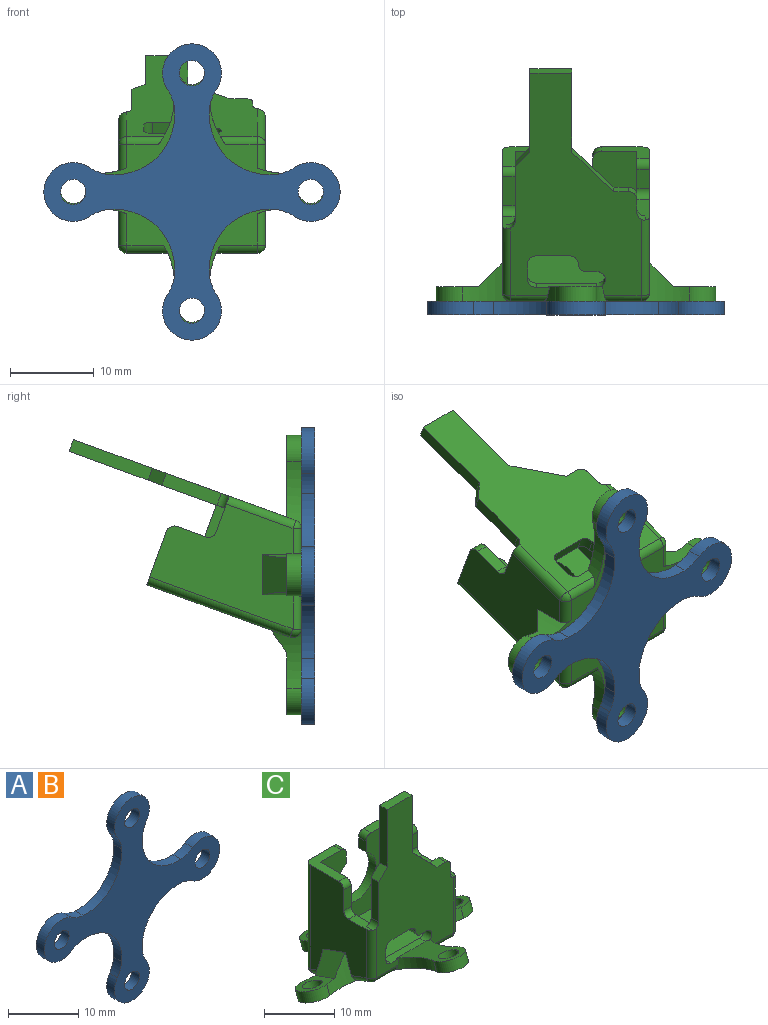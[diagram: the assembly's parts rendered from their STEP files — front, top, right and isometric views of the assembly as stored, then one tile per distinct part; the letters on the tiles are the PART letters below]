
ASSEMBLY  parts=3 mates=1
PART A: 22 faces, bbox 35.3x1.6x35.3 mm
  f0: cylinder r=5mm len=2.39mm, axis (0,1,0), area 4.1mm2, adj f1,f19,f20,f21
  f1: cylinder r=3.5mm len=7mm, axis (0,1,0), area 24.2mm2, adj f0,f2,f20,f21
  f2: cylinder r=5mm len=2.39mm, axis (0,1,0), area 4.1mm2, adj f1,f3,f20,f21
  f3: cylinder r=7.18mm len=7.75mm, axis (0,1,0), area 19.9mm2, adj f2,f4,f20,f21
  f4: cylinder r=5mm len=2.39mm, axis (0,1,0), area 4.1mm2, adj f3,f5,f20,f21
  f5: cylinder r=3.5mm len=7mm, axis (0,1,0), area 24.2mm2, adj f4,f6,f20,f21
  f6: cylinder r=5mm len=2.39mm, axis (0,1,0), area 4.1mm2, adj f5,f7,f20,f21
  f7: cylinder r=7.18mm len=7.75mm, axis (0,1,0), area 19.9mm2, adj f6,f8,f20,f21
  f8: cylinder r=5mm len=2.39mm, axis (0,1,0), area 4.1mm2, adj f7,f9,f20,f21
  f9: cylinder r=3.5mm len=7mm, axis (0,1,0), area 24.2mm2, adj f8,f10,f20,f21
  f10: cylinder r=5mm len=2.39mm, axis (0,1,0), area 4.1mm2, adj f9,f11,f20,f21
  f11: cylinder r=7.18mm len=7.75mm, axis (0,1,0), area 19.9mm2, adj f10,f12,f20,f21
  f12: cylinder r=5mm len=2.39mm, axis (0,1,0), area 4.1mm2, adj f11,f13,f20,f21
  f13: cylinder r=3.5mm len=7mm, axis (0,1,0), area 24.2mm2, adj f12,f14,f20,f21
  f14: cylinder r=5mm len=2.39mm, axis (0,1,0), area 4.1mm2, adj f13,f19,f20,f21
  f15: cylinder r=1.5mm len=3mm, axis (0,1,0), area 15.1mm2, adj f20,f21
  f16: cylinder r=1.5mm len=3mm, axis (0,1,0), area 15.1mm2, adj f20,f21
  f17: cylinder r=1.5mm len=3mm, axis (0,1,0), area 15.1mm2, adj f20,f21
  f18: cylinder r=1.5mm len=3mm, axis (0,1,0), area 15.1mm2, adj f20,f21
  f19: cylinder r=7.18mm len=7.75mm, axis (0,1,0), area 19.9mm2, adj f0,f14,f20,f21
  f20: plane 35.28x35.28mm, normal (0,-1,0), area 333.8mm2, adj f0,f1,f2,f3,f4,f5,f6,f7
  f21: plane 35.28x35.28mm, normal (0,1,0), area 333.8mm2, adj f0,f1,f2,f3,f4,f5,f6,f7
PART B: same geometry as A
PART C: 84 faces, bbox 33.3x31.9x36.7 mm
  f0: plane 18.14x11.25mm, normal (-1,0,0), area 138.6mm2, adj f8,f21,f22,f36,f37,f44,f45,f64
  f1: plane 28.19x15.51mm, normal (0,-1,0), area 258.5mm2, adj f4,f5,f6,f17,f20,f23,f24,f25
  f2: plane 18.18x15.53mm, normal (0,1,0), area 205.4mm2, adj f8,f9,f14,f15,f16,f41,f42,f43
  f3: plane 18.14x11.25mm, normal (1,0,0), area 131.4mm2, adj f9,f18,f19,f38,f39,f40,f43,f57
  f4: plane 7.25x1.5mm, normal (0,0,1), area 9.1mm2, adj f1,f5,f7,f35,f51,f52
  f5: cylinder r=1mm len=2mm, axis (0,-1,0), area 4.6mm2, adj f1,f4,f7,f25,f51
  f6: plane 1.75x1.5mm, normal (0,0,1), area 2.6mm2, adj f1,f7,f29,f48
  f7: plane 27.38x16.5mm, normal (0,1,0), area 244.8mm2, adj f4,f5,f6,f11,f12,f13,f17,f18
  f8: plane 6.75x5.75mm, normal (0,0,1), area 16.3mm2, adj f0,f2,f10,f12,f37,f41,f44
  f9: plane 5.75x4.05mm, normal (0,0,1), area 12.2mm2, adj f2,f3,f10,f11,f40,f42,f43
  f10: plane 14.5x13.25mm, normal (0,-1,0), area 131.3mm2, adj f8,f9,f11,f12,f13,f14,f15,f16
  f11: plane 13.25x10.25mm, normal (-1,0,0), area 105.7mm2, adj f7,f9,f10,f13,f18,f19,f39,f40
  f12: plane 13.25x10.25mm, normal (1,0,0), area 113.4mm2, adj f7,f8,f10,f13,f21,f22,f36,f37
  f13: plane 14.5x10.25mm, normal (0,0,1), area 148.6mm2, adj f7,f10,f11,f12
  f14: cylinder r=4mm len=8mm, axis (0,1,0), area 31.4mm2, adj f2,f10,f15,f16
  f15: plane 1.89x1.5mm, normal (-1,0,0), area 2.8mm2, adj f2,f10,f14,f42
  f16: plane 1.89x1.5mm, normal (1,0,0), area 2.8mm2, adj f2,f10,f14,f41
  f17: plane 1.63x1.5mm, normal (1,0,0), area 2.4mm2, adj f1,f7,f47,f48
  f18: plane 7.07x1.5mm, normal (0,0,1), area 9.1mm2, adj f3,f7,f11,f38,f39,f47
  f19: plane 2.5x1.5mm, normal (0,-1,0), area 3.8mm2, adj f3,f11,f39,f40
  f20: plane 6.98x1.5mm, normal (-1,0,0), area 10.5mm2, adj f1,f7,f30,f46
  f21: plane 3.6x1.5mm, normal (0,-1,0), area 5.4mm2, adj f0,f12,f36,f37
  f22: plane 4.37x1.5mm, normal (0,0,1), area 5.1mm2, adj f0,f7,f12,f36,f45,f46
  f23: plane 4x1.5mm, normal (0,0,-1), area 6mm2, adj f1,f7,f33,f34
  f24: plane 2x1.5mm, normal (1,0,0), area 3mm2, adj f1,f7,f34,f35
  f25: plane 1.5x1.25mm, normal (0,0,-1), area 1.9mm2, adj f1,f5,f7,f32
  f26: plane 10x1.5mm, normal (1,0,0), area 15mm2, adj f1,f7,f28,f29
  f27: plane 10x1.5mm, normal (-1,0,0), area 15mm2, adj f1,f7,f28,f30
  f28: plane 5x1.5mm, normal (0,0,1), area 7.5mm2, adj f1,f7,f26,f27
  f29: plane 5x5mm, normal (0.71,0,0.71), area 10.6mm2, adj f1,f6,f7,f26
  f30: plane 1.75x1.75mm, normal (-0.71,0,0.71), area 3.7mm2, adj f1,f7,f20,f27
  f31: plane 33.28x31.28mm, normal (0,-0.34,-0.94), area 335.5mm2, adj f49,f50,f52,f53,f54,f55,f57,f58
  f32: cylinder r=1mm len=1.5mm, axis (0,-1,0), area 2.4mm2, adj f1,f7,f25,f33
  f33: cylinder r=1mm len=1.5mm, axis (0,1,0), area 2.4mm2, adj f1,f7,f23,f32
  f34: cylinder r=1mm len=1.5mm, axis (0,1,0), area 2.4mm2, adj f1,f7,f23,f24
  f35: cylinder r=1mm len=1.5mm, axis (0,-1,0), area 2.4mm2, adj f1,f4,f7,f24
  f36: cylinder r=1mm len=1.5mm, axis (1,0,0), area 2.4mm2, adj f0,f12,f21,f22
  f37: cylinder r=1mm len=1.5mm, axis (-1,0,0), area 2.4mm2, adj f0,f8,f12,f21
  f38: cylinder r=1mm len=9.68mm, axis (0,0,-1), area 15mm2, adj f1,f3,f18,f47,f76
  f39: cylinder r=1mm len=1.5mm, axis (-1,0,0), area 2.4mm2, adj f3,f11,f18,f19
  f40: cylinder r=1mm len=1.5mm, axis (-1,0,0), area 2.4mm2, adj f3,f9,f11,f19
  f41: cylinder r=1mm len=1.5mm, axis (0,-1,0), area 2.4mm2, adj f2,f8,f10,f16
  f42: cylinder r=1mm len=1.5mm, axis (0,1,0), area 2.4mm2, adj f2,f9,f10,f15
  f43: cylinder r=1mm len=18.14mm, axis (0,0,1), area 28.5mm2, adj f2,f3,f9,f80
  f44: cylinder r=1mm len=18.14mm, axis (0,0,-1), area 28.5mm2, adj f0,f2,f8,f70
  f45: cylinder r=1mm len=8.58mm, axis (0,0,1), area 13.3mm2, adj f0,f1,f22,f46,f73
  f46: cylinder r=1mm len=1.5mm, axis (0,-1,0), area 2.3mm2, adj f1,f7,f20,f22,f45
  f47: cylinder r=1mm len=1.5mm, axis (0,1,0), area 2.3mm2, adj f1,f7,f17,f18,f38
  f48: cylinder r=1mm len=1.5mm, axis (0,-1,0), area 2.4mm2, adj f1,f6,f7,f17
  f49: cylinder r=1.5mm len=3.42mm, axis (0,-0.34,-0.94), area 16.5mm2, adj f31,f51
  f50: cylinder r=2.5mm len=5mm, axis (0,-0.34,-0.94), area 16.1mm2, adj f31,f51,f52,f53
  f51: plane 9.5x6.46mm, normal (0,0.34,0.94), area 39mm2, adj f1,f4,f5,f49,f50,f52,f53
  f52: cylinder r=9mm len=8.07mm, axis (0,-0.34,-0.94), area 12.7mm2, adj f1,f4,f31,f50,f51,f72
  f53: cylinder r=9mm len=8.07mm, axis (0,-0.34,-0.94), area 12.7mm2, adj f1,f31,f50,f51,f75
  f54: cylinder r=1.5mm len=3.42mm, axis (0,-0.34,-0.94), area 16.5mm2, adj f31,f56
  f55: cylinder r=2.5mm len=5.3mm, axis (0,-0.34,-0.94), area 16.1mm2, adj f31,f56,f57,f58
  f56: plane 5.04x4.7mm, normal (0,0.34,0.94), area 14.3mm2, adj f54,f55,f57,f58,f81
  f57: cylinder r=9mm len=5.73mm, axis (0,-0.34,-0.94), area 12.7mm2, adj f3,f31,f55,f56,f77,f81
  f58: cylinder r=9mm len=5.73mm, axis (0,-0.34,-0.94), area 12.7mm2, adj f3,f31,f55,f56,f79,f81
  f59: cylinder r=2.5mm len=5mm, axis (0,-0.34,-0.94), area 16.1mm2, adj f31,f61,f62,f63
  f60: cylinder r=1.5mm len=3.42mm, axis (0,-0.34,-0.94), area 16.5mm2, adj f31,f61
  f61: plane 6.96x5mm, normal (0,0.34,0.94), area 24.5mm2, adj f59,f60,f62,f63,f83
  f62: cylinder r=9mm len=7.85mm, axis (0,-0.34,-0.94), area 13.1mm2, adj f2,f31,f59,f61,f69,f83
  f63: cylinder r=9mm len=7.85mm, axis (0,-0.34,-0.94), area 13.1mm2, adj f2,f31,f59,f61,f78,f83
  f64: cylinder r=9mm len=5.73mm, axis (0,-0.34,-0.94), area 12.7mm2, adj f0,f31,f66,f67,f74,f82
  f65: cylinder r=9mm len=5.73mm, axis (0,-0.34,-0.94), area 12.7mm2, adj f0,f31,f66,f67,f71,f82
  f66: plane 5.04x4.7mm, normal (0,0.34,0.94), area 14.3mm2, adj f64,f65,f67,f68,f82
  f67: cylinder r=2.5mm len=5.3mm, axis (0,-0.34,-0.94), area 16.1mm2, adj f31,f64,f65,f66
  f68: cylinder r=1.5mm len=3.42mm, axis (0,-0.34,-0.94), area 16.5mm2, adj f31,f66
  f69: cylinder r=1mm len=4.89mm, axis (-1,0,0), area 9.1mm2, adj f2,f31,f62,f70
  f70: sphere r=1mm, area 1.9mm2, adj f44,f69,f71
  f71: cylinder r=1mm len=4.15mm, axis (0,0.94,-0.34), area 6.2mm2, adj f0,f31,f65,f70
  f72: cylinder r=1mm len=4.39mm, axis (1,0,0), area 5mm2, adj f1,f31,f52,f73
  f73: sphere r=1mm, area 1.2mm2, adj f45,f72,f74
  f74: cylinder r=1mm len=3.28mm, axis (0,0.94,-0.34), area 4.7mm2, adj f0,f31,f64,f73
  f75: cylinder r=1mm len=4.39mm, axis (1,0,0), area 5mm2, adj f1,f31,f53,f76
  f76: sphere r=1mm, area 1.2mm2, adj f38,f75,f77
  f77: cylinder r=1mm len=3.28mm, axis (0,0.94,-0.34), area 4.7mm2, adj f3,f31,f57,f76
  f78: cylinder r=1mm len=4.89mm, axis (-1,0,0), area 9.1mm2, adj f2,f31,f63,f80
  f79: cylinder r=1mm len=4.15mm, axis (0,0.94,-0.34), area 6.2mm2, adj f3,f31,f58,f80
  f80: sphere r=1mm, area 1.9mm2, adj f43,f78,f79
  f81: plane 5.23x4.25mm, normal (0.71,0.24,0.66), area 17.5mm2, adj f3,f56,f57,f58
  f82: plane 5.23x4.25mm, normal (-0.71,0.24,0.66), area 17.5mm2, adj f0,f64,f65,f66
  f83: plane 6.62x2.68mm, normal (0,0.82,0.57), area 17.8mm2, adj f2,f61,f62,f63
PLACE A t=(-1.76,-0.33,-0.18)mm
PLACE B t=(-1.76,-0.33,-0.18)mm
PLACE C rot(axis=(-1,0,0),70deg) t=(-1.76,1.93,-0.04)mm
MATE fastened C.f31 <-> B.f21  axis (0,-1,0) through (-1.76,-0.33,-0.18)mm
